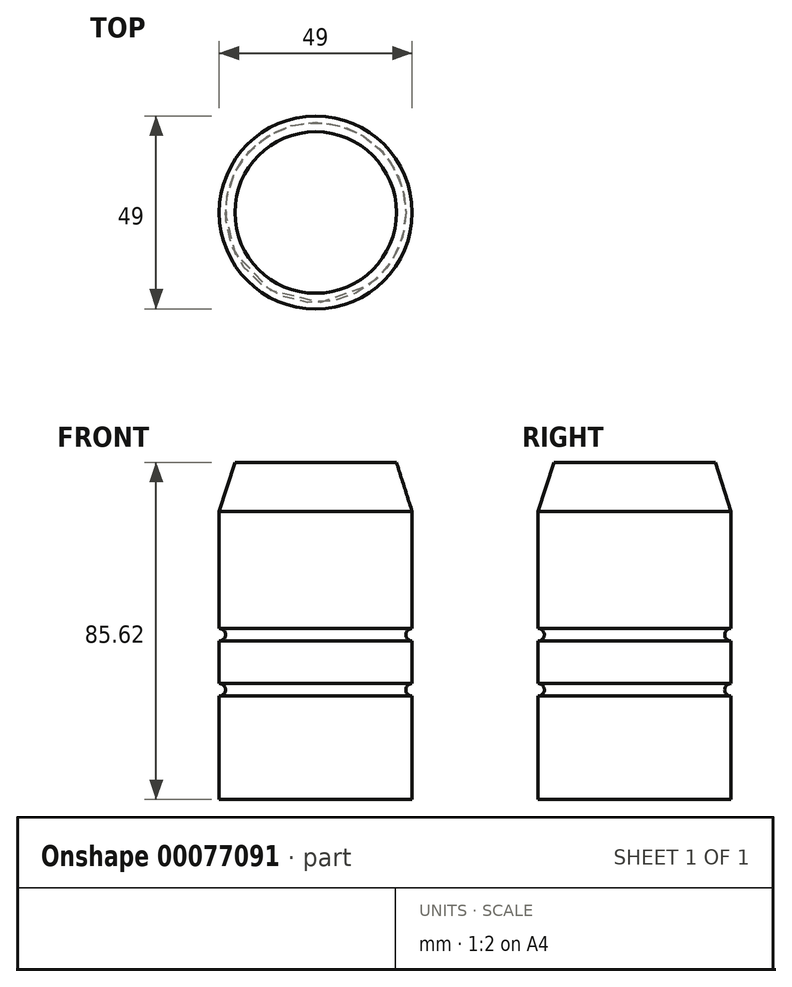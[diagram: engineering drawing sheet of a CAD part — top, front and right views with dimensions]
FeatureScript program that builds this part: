
annotation { "Feature Type Name" : "Feature", "Feature Type Description" : "" }
export const myFeature = defineFeature(function(context is Context, id is Id, definition is map)
    precondition{}
    {
        {
            var Q0;
            Q0=qCreatedBy(makeId("Front.planeOp"),FACE);
            var sketch = newSketch(context, id + "F0", { "sketchPlane" : qUnion([Q0])});
            skPoint(sketch, "E0.endSnap0", {"position": v(28.18, 0) * mm});
            skLineSegment(sketch, "E1.top", {"start": v(-26.47, -30) * mm, "end": v(-27.67, -30) * mm});
            skLineSegment(sketch, "E2", {"start": v(0, 61.87) * mm, "end": v(0, 62.09) * mm});
            skLineSegment(sketch, "E3", {"start": v(-26.47, -30) * mm, "end": v(-25.75, -30) * mm});
            skLineSegment(sketch, "E4", {"start": v(0, 61.87) * mm, "end": v(0, 60.17) * mm});
            skLineSegment(sketch, "E5", {"start": v(0, 68.96) * mm, "end": v(0, -42.27) * mm, "construction": true});
            skLineSegment(sketch, "E6.bottom", {"start": v(-22.17, 31.94) * mm, "end": v(-22.17, 31.94) * mm});
            skLineSegment(sketch, "E6.top", {"start": v(-24.5, -53.68) * mm, "end": v(0, -53.68) * mm});
            skLineSegment(sketch, "E6.right", {"start": v(0, 31.94) * mm, "end": v(0, -53.68) * mm});
            skLineSegment(sketch, "E7", {"start": v(-24.5, 19.45) * mm, "end": v(-20.51, 31.94) * mm});
            skArc(sketch, "E8", {"start": v(-24.5, -13.43) * mm, "mid": v(-22.91, -11.84) * mm, "end": v(-24.5, -10.25) * mm});
            skLineSegment(sketch, "E9.trimOffspring", {"start": v(-20.51, 31.94) * mm, "end": v(0, 31.94) * mm});
            skLineSegment(sketch, "E10.trimOffspring", {"start": v(-24.5, 19.45) * mm, "end": v(-24.5, -10.25) * mm});
            skArc(sketch, "E11", {"start": v(-24.5, -27.42) * mm, "mid": v(-22.9, -25.84) * mm, "end": v(-24.5, -24.25) * mm});
            skLineSegment(sketch, "E12.trimOffspring", {"start": v(-24.5, -27.42) * mm, "end": v(-24.5, -53.68) * mm});
            skPoint(sketch, "E13.center.orphan", {"position": v(0, 0) * mm});
            skLineSegment(sketch, "E14", {"start": v(-24.5, -13.43) * mm, "end": v(-24.5, -24.25) * mm});
            skSolve(sketch);
        }
        {
            var Q0;
            Q0=makeQuery(id+"F0.imprint","IMPRINT",FACE,{"disambiguationData":[TD([[makeQuery(id+"F0.imprint","IMPRINT",EDGE,{"derivedFrom":sQuery(id+"F0.wireOp",EDGE,"E6.top")}),1.0]])]});
            var Q1;
            Q1=sQuery(id+"F0.wireOp",EDGE,"E5");
            revolve(context, id + "F1", {"entities" : qUnion([Q0]), "axis" : qUnion([Q1]), "revolveType" : RevolveType.FULL});
        }
    });
